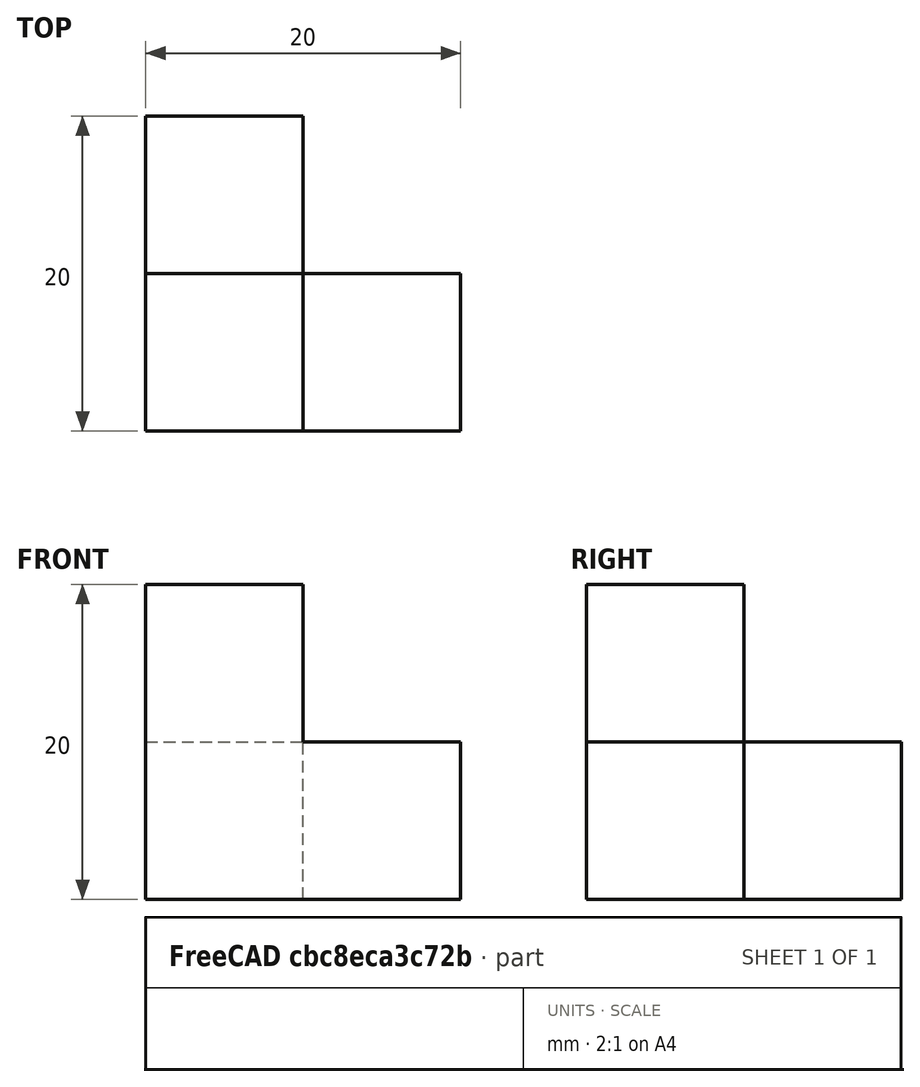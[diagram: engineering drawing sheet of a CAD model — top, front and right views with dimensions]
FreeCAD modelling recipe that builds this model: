
FCSTD DOCUMENT  (FreeCAD 1.0R39319 (Git))
Label: ojt1_t05r01_unions
License: All rights reserved
LicenseURL: https://en.wikipedia.org/wiki/All_rights_reserved
objects: Part::Box×4, Part::MultiFuse×1
note: 5 computed .brp shape members not serialized (recipe doc carries the construction recipe); baked Part::Feature solids carry a one-line shape summary decoded from their .brp

FEATURE [Part::Box] Box  label="Cub"
  AttacherType = Attacher::AttachEngine3D
  Height = 10
  Length = 10
  Width = 10
FEATURE [Part::Box] Box001  label="Cub001"
  AttacherType = Attacher::AttachEngine3D
  Height = 10
  Length = 10
  Placement = pos=(10,0,0) rot=(0,0,1;0rad)
  Width = 10
FEATURE [Part::Box] Box002  label="Cub002"
  AttacherType = Attacher::AttachEngine3D
  Height = 10
  Length = 10
  Placement = pos=(0,10,0) rot=(0,0,1;0rad)
  Width = 10
FEATURE [Part::Box] Box003  label="Cub003"
  AttacherType = Attacher::AttachEngine3D
  Height = 10
  Length = 10
  Placement = pos=(0,0,10) rot=(0,0,1;0rad)
  Width = 10
FEATURE [Part::MultiFuse] Fusion
  Refine = true
  Shapes = -> [Box,Box001,Box002,Box003]
